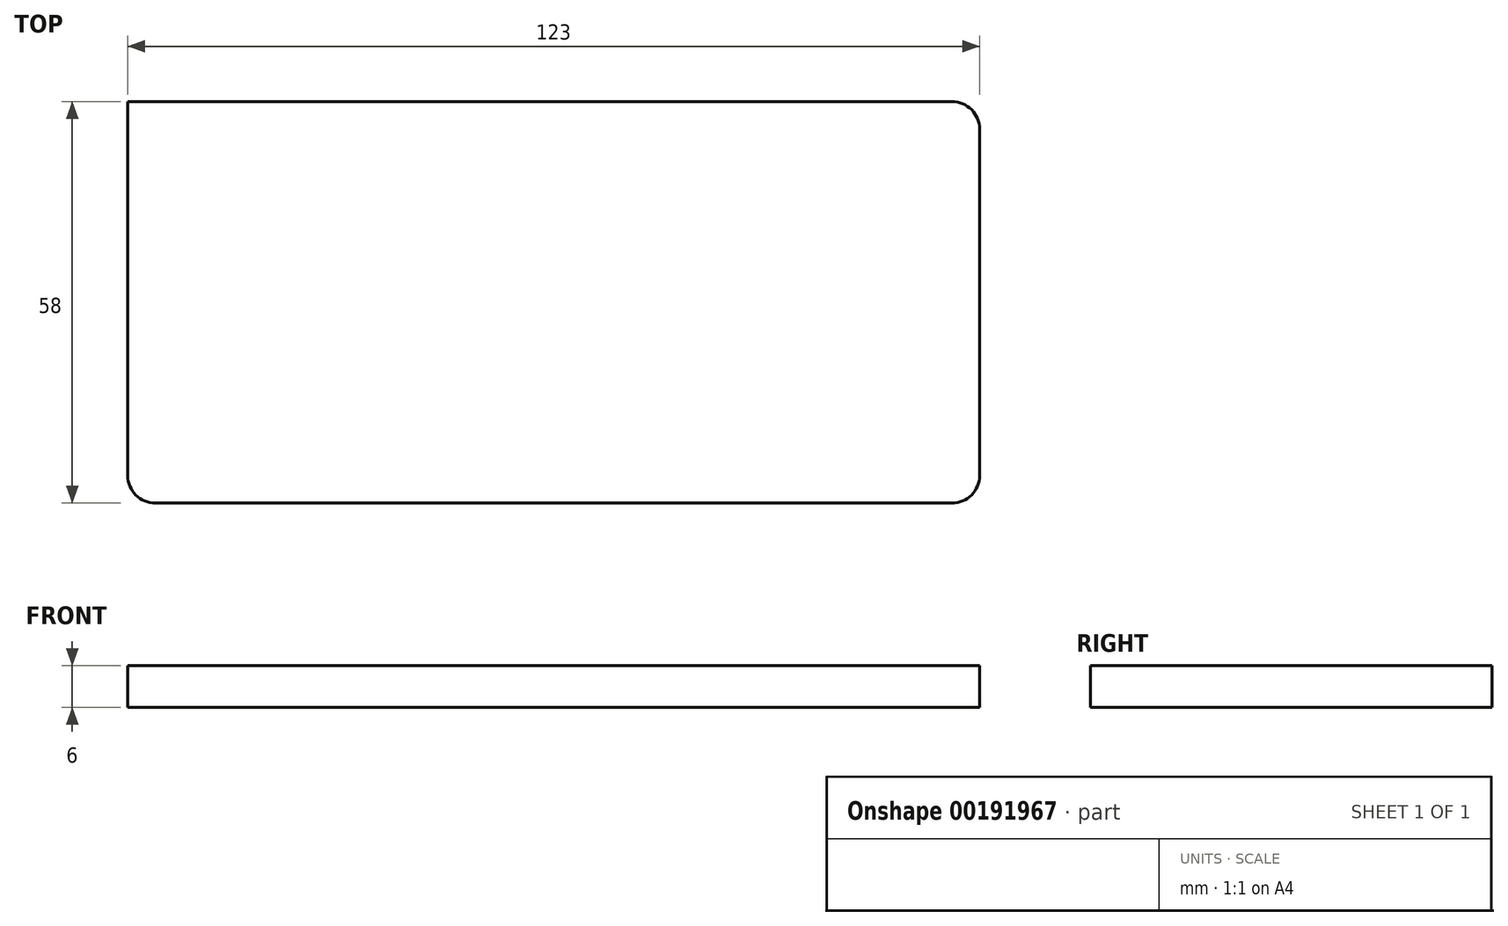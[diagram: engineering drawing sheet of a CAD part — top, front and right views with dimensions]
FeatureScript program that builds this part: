
annotation { "Feature Type Name" : "Feature", "Feature Type Description" : "" }
export const myFeature = defineFeature(function(context is Context, id is Id, definition is map)
    precondition{}
    {
        {
            var Q0;
            Q0=qCreatedBy(makeId("Top.planeOp"),FACE);
            var sketch = newSketch(context, id + "F0", { "sketchPlane" : qUnion([Q0])});
            skLineSegment(sketch, "E0.bottom", {"start": v(61.5, -29) * mm, "end": v(-61.5, -29) * mm});
            skLineSegment(sketch, "E0.top", {"start": v(61.5, 29) * mm, "end": v(-61.5, 29) * mm});
            skLineSegment(sketch, "E0.left", {"start": v(61.5, -29) * mm, "end": v(61.5, 29) * mm});
            skLineSegment(sketch, "E0.right", {"start": v(-61.5, -29) * mm, "end": v(-61.5, 29) * mm});
            skPoint(sketch, "E0.middle", {"position": v(0, 0) * mm});
            skSolve(sketch);
        }
        {
            var Q0;
            Q0 = qSketchRegion(id + "F0", true);
            extrude(context, id + "F1", {"entities" : qUnion([Q0]), "depth" : 6 * mm});
        }
        {
            var Q0;
            Q0=makeQuery(id+"F1.opExtrude","SWEPT_EDGE",EDGE,{"disambiguationData":[OSD([sQuery(id+"F0.wireOp",EDGE,"E0.bottom"),sQuery(id+"F0.wireOp",EDGE,"E0.left")])]});
            var Q1;
            Q1=makeQuery(id+"F1.opExtrude","SWEPT_EDGE",EDGE,{"disambiguationData":[OSD([sQuery(id+"F0.wireOp",EDGE,"E0.bottom"),sQuery(id+"F0.wireOp",EDGE,"E0.right")])]});
            var Q2;
            Q2=makeQuery(id+"F1.opExtrude","SWEPT_EDGE",EDGE,{"disambiguationData":[OSD([sQuery(id+"F0.wireOp",EDGE,"E0.top"),sQuery(id+"F0.wireOp",EDGE,"E0.left")])]});
            fillet(context, id + "F2", {"entities" : qUnion([Q0, Q1, Q2]), "radius" : 4 * mm, "tangentPropagation" : true, "allowEdgeOverflow" : false});
        }
    });
